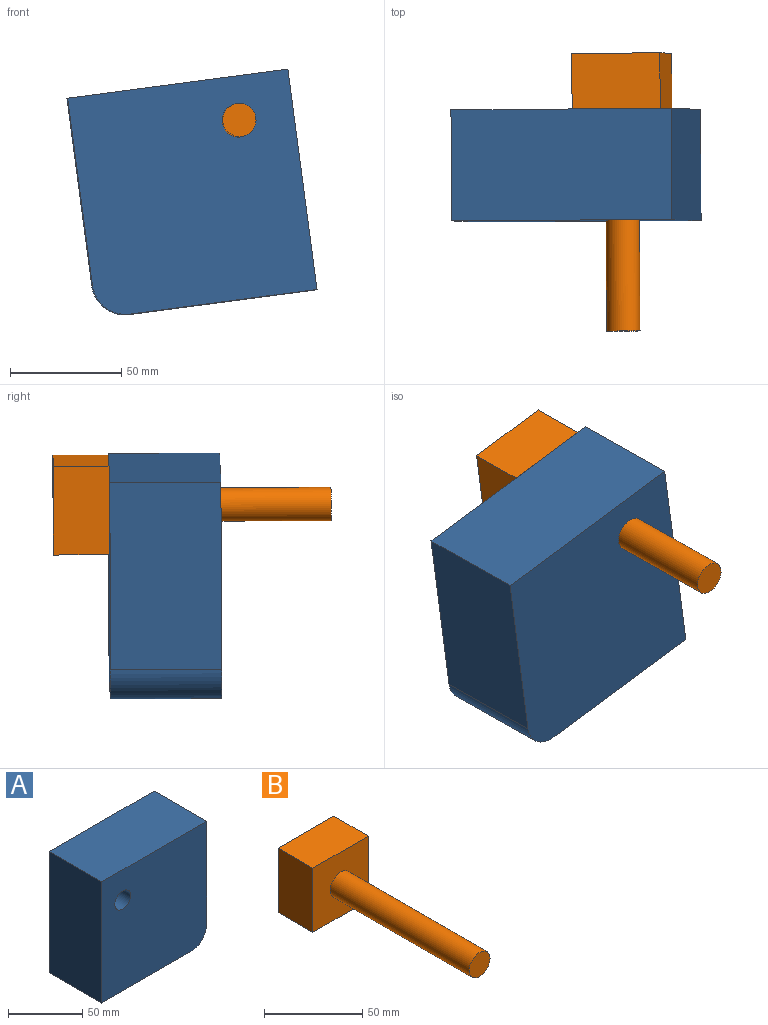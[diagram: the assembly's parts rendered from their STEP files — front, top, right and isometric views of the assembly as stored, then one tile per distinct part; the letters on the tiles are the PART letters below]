
ASSEMBLY  parts=2 mates=2
PART A: 8 faces, bbox 100x50x100 mm
  f0: plane 100x50mm, normal (0,0,1), area 5000mm2, adj f1,f4,f5,f6
  f1: plane 100x50mm, normal (-1,0,0), area 5000mm2, adj f0,f2,f5,f6
  f2: plane 85x50mm, normal (0,0,-1), area 4250mm2, adj f1,f5,f6,f7
  f3: cylinder r=7.5mm len=50mm, axis (0,1,0), area 2356.2mm2, adj f5,f6
  f4: plane 85x50mm, normal (1,0,0), area 4250mm2, adj f0,f5,f6,f7
  f5: plane 100x100mm, normal (0,-1,0), area 9775mm2, adj f0,f1,f2,f3,f4,f7
  f6: plane 100x100mm, normal (0,1,0), area 9775mm2, adj f0,f1,f2,f3,f4,f7
  f7: cylinder r=15mm len=50mm, axis (0,-1,0), area 1178.1mm2, adj f2,f4,f5,f6
PART B: 8 faces, bbox 40x125x40 mm
  f0: plane 40x25mm, normal (0,0,-1), area 1000mm2, adj f1,f3,f4,f5
  f1: plane 40x25mm, normal (1,0,0), area 1000mm2, adj f0,f2,f4,f5
  f2: plane 40x25mm, normal (0,0,1), area 1000mm2, adj f1,f3,f4,f5
  f3: plane 40x25mm, normal (-1,0,0), area 1000mm2, adj f0,f2,f4,f5
  f4: plane 40x40mm, normal (0,-1,0), area 1423.3mm2, adj f0,f1,f2,f3,f6
  f5: plane 40x40mm, normal (0,1,0), area 1600mm2, adj f0,f1,f2,f3
  f6: cylinder r=7.5mm len=100mm, axis (0,1,0), area 4712.4mm2, adj f4,f7
  f7: plane 15x15mm, normal (0,-1,0), area 176.7mm2, adj f6
PLACE A rot(axis=(-0.01,1,0),82.5deg) t=(-31.92,108.03,44.54)mm fixed
PLACE B rot(axis=(-0.01,1,0),82.5deg) t=(-11.3,145.8,77.41)mm
MATE planar A.f6 <-> B.f4  axis (-0.01,1,0) through (-32.25,133.03,44.1)mm
MATE cylindrical B.f6 <-> A.f3  axis (-0.01,1,0) through (-10.91,83.3,77.67)mm
